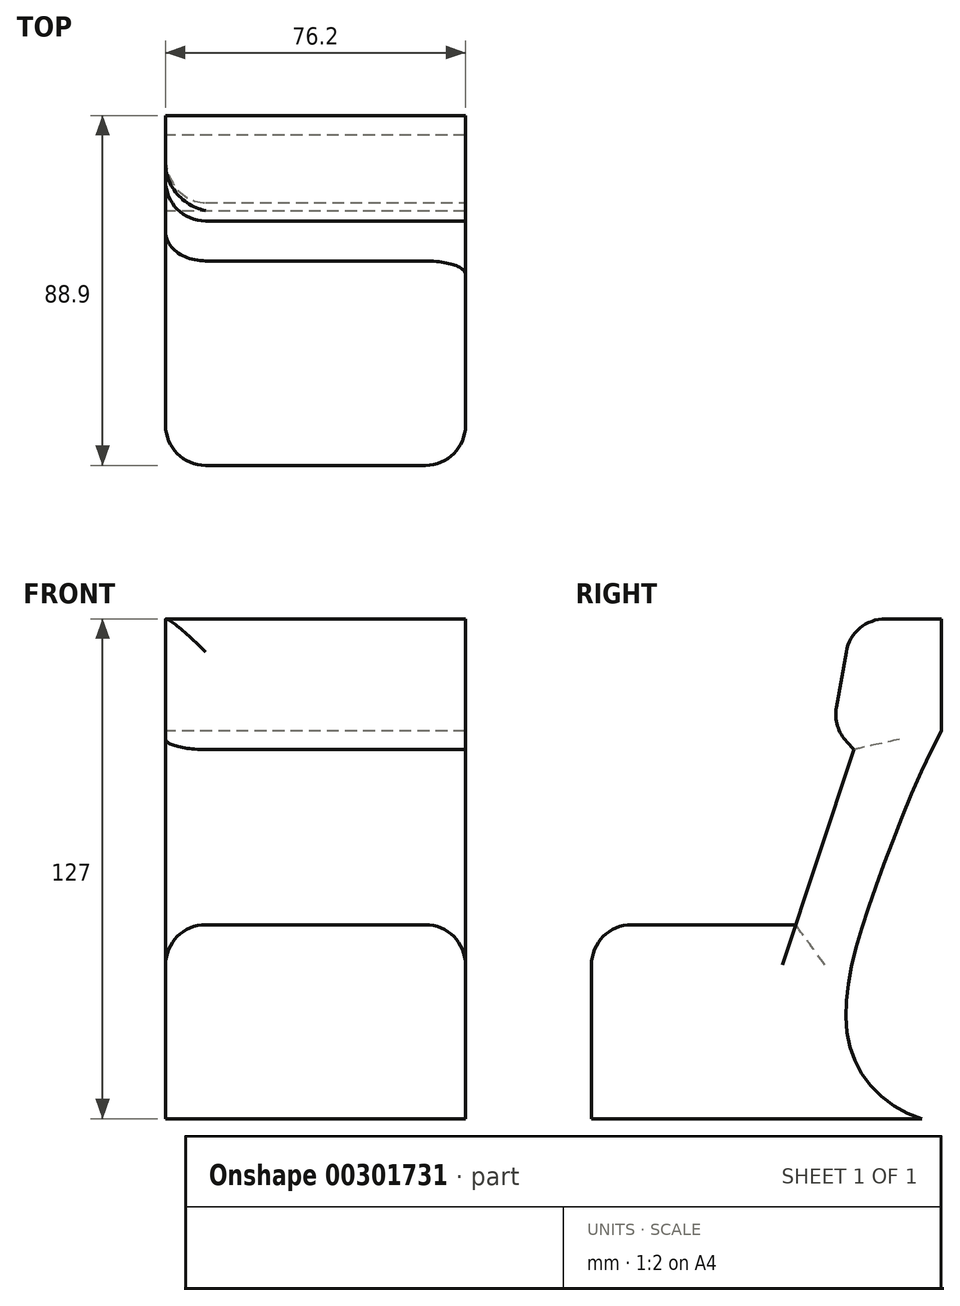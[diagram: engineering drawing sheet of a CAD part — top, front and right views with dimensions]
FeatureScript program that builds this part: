
annotation { "Feature Type Name" : "Feature", "Feature Type Description" : "" }
export const myFeature = defineFeature(function(context is Context, id is Id, definition is map)
    precondition{}
    {
        {
            var Q0;
            Q0=qCreatedBy(makeId("Top.planeOp"),FACE);
            var sketch = newSketch(context, id + "F0", { "sketchPlane" : qUnion([Q0])});
            skLineSegment(sketch, "E0.bottom", {"start": v(-38.1, 44.45) * mm, "end": v(38.1, 44.45) * mm});
            skLineSegment(sketch, "E0.top", {"start": v(-38.1, -44.45) * mm, "end": v(38.1, -44.45) * mm});
            skLineSegment(sketch, "E0.left", {"start": v(-38.1, 44.45) * mm, "end": v(-38.1, -44.45) * mm});
            skLineSegment(sketch, "E0.right", {"start": v(38.1, 44.45) * mm, "end": v(38.1, -44.45) * mm});
            skPoint(sketch, "E0.middle", {"position": v(0, 0) * mm});
            skSolve(sketch);
        }
        {
            var Q0;
            Q0=makeQuery(id+"F0.imprint","IMPRINT",FACE,{"disambiguationData":[TD([[makeQuery(id+"F0.imprint","IMPRINT",EDGE,{"derivedFrom":sQuery(id+"F0.wireOp",EDGE,"E0.bottom")}),-1.0]])]});
            extrude(context, id + "F1", {"entities" : qUnion([Q0]), "depth" : 127 * mm});
        }
        {
            var Q0;
            Q0=makeQuery(id+"F1.opExtrude","SWEPT_FACE",FACE,{"disambiguationData":[OSD([sQuery(id+"F0.wireOp",EDGE,"E0.right")])]});
            var sketch = newSketch(context, id + "F2", { "sketchPlane" : qUnion([Q0])});
            skSolve(sketch);
        }
        {
            var Q0;
            {var subQ0=sQuery(id+"F0.wireOp",EDGE,"E0.right");Q0=makeQuery(id+"F2.imprint","IMPRINT",FACE,{"disambiguationData":[TD([[makeQuery(id+"F2.imprint","IMPRINT",EDGE,{"derivedFrom":makeQuery(id+"F1.opExtrude","CAP_EDGE",EDGE,{"disambiguationData":[OSD([subQ0])],"isStart":true})}),-1.0]])]});}
            var sketch = newSketch(context, id + "F3", { "sketchPlane" : qUnion([Q0])});
            skLineSegment(sketch, "E1", {"start": v(7.48, 49.25) * mm, "end": v(-45.8, 49.25) * mm});
            skLineSegment(sketch, "E2", {"start": v(-45.8, 49.25) * mm, "end": v(-45.8, 129.88) * mm});
            skLineSegment(sketch, "E3", {"start": v(22.28, 129.88) * mm, "end": v(22.28, 127.37) * mm});
            skLineSegment(sketch, "E4", {"start": v(22.28, 129.88) * mm, "end": v(-45.8, 129.88) * mm});
            skLineSegment(sketch, "E5", {"start": v(22.28, 129.88) * mm, "end": v(16.9, 99.46) * mm});
            skLineSegment(sketch, "E6", {"start": v(16.9, 99.46) * mm, "end": v(22.28, 93.8) * mm});
            skLineSegment(sketch, "E7", {"start": v(22.28, 93.8) * mm, "end": v(7.48, 49.25) * mm});
            skPoint(sketch, "E8.start.orphan", {"position": v(22.28, 103.53) * mm});
            skSolve(sketch);
        }
        {
            var Q0;
            Q0=makeQuery(id+"F1.opExtrude","SWEPT_EDGE",EDGE,{"disambiguationData":[OSD([sQuery(id+"F0.wireOp",EDGE,"E0.top"),sQuery(id+"F0.wireOp",EDGE,"E0.left")])]});
            var Q1;
            Q1=makeQuery(id+"F1.opExtrude","SWEPT_EDGE",EDGE,{"disambiguationData":[OSD([sQuery(id+"F0.wireOp",EDGE,"E0.top"),sQuery(id+"F0.wireOp",EDGE,"E0.right")])]});
            fillet(context, id + "F4", {"entities" : qUnion([Q0, Q1]), "radius" : 10.16 * mm, "tangentPropagation" : true, "allowEdgeOverflow" : false});
        }
        {
            var Q0;
            Q0 = qSketchRegion(id + "F3", true);
            extrude(context, id + "F5", {"entities" : qUnion([Q0]), "operationType" : NewBodyOperationType.REMOVE, "endBound" : BoundingType.THROUGH_ALL, "oppositeDirection" : true, "depth" : 25.4 * mm});
        }
        {
            var Q0;
            Q0=makeQuery(id+"F1.opExtrude","SWEPT_FACE",FACE,{"disambiguationData":[OSD([sQuery(id+"F0.wireOp",EDGE,"E0.left")])]});
            var sketch = newSketch(context, id + "F6", { "sketchPlane" : qUnion([Q0])});
            skFitSpline(sketch, "E9", {"points": [v(-48.98, 121.86) * mm, v(-37.37, 73.23) * mm, v(-19.17, 29.61) * mm, v(-41.45, 0) * mm, v(-93.22, 20.83) * mm, v(-48.98, 121.86) * mm]});
            skSolve(sketch);
        }
        {
            var Q0;
            {var subQ0=sQuery(id+"F6.wireOp",EDGE,"E9");var subQ1=sQuery(id+"F0.wireOp",EDGE,"E0.left");var subQ4=makeQuery(id+"F1.opExtrude","CAP_EDGE",EDGE,{"disambiguationData":[OSD([subQ1])],"isStart":true});var subQ5=makeQuery(id+"F6.imprint","INTERSECT",VERTEX,{"derivedFrom":[subQ4,subQ0]});Q0=makeQuery(id+"F6.imprint","IMPRINT",FACE,{"disambiguationData":[TD([[makeQuery(id+"F6.imprint","IMPRINT",EDGE,{"disambiguationData":[TD([[subQ5,-1.0]])],"derivedFrom":subQ0}),-1.0]])]});}
            extrude(context, id + "F7", {"entities" : qUnion([Q0]), "operationType" : NewBodyOperationType.REMOVE, "oppositeDirection" : true, "depth" : 93.98 * mm});
        }
        {
            var Q0;
            Q0=qCreatedBy(makeId("Right.planeOp"),FACE);
            cPlane(context, id + "F8", {"entities" : qUnion([Q0]), "cplaneType" : CPlaneType.OFFSET, "offset" : 192.02 * mm, "oppositeDirection" : true, "width" : 152.4 * mm, "height" : 152.4 * mm});
        }
        {
            var Q0;
            Q0=qCreatedBy(id+"F8.planeOp",FACE);
            var sketch = newSketch(context, id + "F9", { "sketchPlane" : qUnion([Q0])});
            skFitSpline(sketch, "E10", {"points": [v(58.83, 110.77) * mm, v(29.42, 63.43) * mm, v(24.82, 10.57) * mm, v(55.62, 4.6) * mm, v(58.83, 110.77) * mm]});
            skSolve(sketch);
        }
        {
            var Q0;
            Q0=makeQuery(id+"F9.imprint","IMPRINT",FACE,{"disambiguationData":[TD([[makeQuery(id+"F9.imprint","IMPRINT",EDGE,{"derivedFrom":sQuery(id+"F9.wireOp",EDGE,"E10")}),1.0]])]});
            extrude(context, id + "F10", {"entities" : qUnion([Q0]), "operationType" : NewBodyOperationType.REMOVE, "depth" : 239 * mm});
        }
        {
            var Q0;
            Q0=makeQuery(id+"F5.boolean.opBoolean","COPY",EDGE,{"derivedFrom":makeQuery(id+"F5.opExtrude","SWEPT_EDGE",EDGE,{"disambiguationData":[OSD([sQuery(id+"F3.wireOp",EDGE,"E5"),sQuery(id+"F3.wireOp",EDGE,"E6")])]})});
            var Q1;
            Q1=makeQuery(id+"F5.boolean.opBoolean","INTERSECT",EDGE,{"derivedFrom":[makeQuery(id+"F1.opExtrude","SWEPT_FACE",FACE,{"disambiguationData":[OSD([sQuery(id+"F0.wireOp",EDGE,"E0.left")])]}),makeQuery(id+"F5.opExtrude","SWEPT_FACE",FACE,{"disambiguationData":[OSD([sQuery(id+"F3.wireOp",EDGE,"E7")])]})]});
            var Q2;
            Q2=makeQuery(id+"F5.boolean.opBoolean","COPY",EDGE,{"derivedFrom":makeQuery(id+"F5.opExtrude","CAP_EDGE",EDGE,{"disambiguationData":[OSD([sQuery(id+"F3.wireOp",EDGE,"E7")])],"isStart":true})});
            var Q3;
            Q3=makeQuery(id+"F5.boolean.opBoolean","INTERSECT",EDGE,{"derivedFrom":[makeQuery(id+"F1.opExtrude","SWEPT_FACE",FACE,{"disambiguationData":[OSD([sQuery(id+"F0.wireOp",EDGE,"E0.left")])]}),makeQuery(id+"F5.opExtrude","SWEPT_FACE",FACE,{"disambiguationData":[OSD([sQuery(id+"F3.wireOp",EDGE,"E1")])]})]});
            var Q4;
            Q4=makeQuery(id+"F5.boolean.opBoolean","INTERSECT",EDGE,{"derivedFrom":[makeQuery(id+"F1.opExtrude","SWEPT_FACE",FACE,{"disambiguationData":[OSD([sQuery(id+"F0.wireOp",EDGE,"E0.left")])]}),makeQuery(id+"F5.opExtrude","SWEPT_FACE",FACE,{"disambiguationData":[OSD([sQuery(id+"F3.wireOp",EDGE,"E5")])]})]});
            var Q5;
            Q5=makeQuery(id+"F5.boolean.opBoolean","INTERSECT",EDGE,{"derivedFrom":[makeQuery(id+"F1.opExtrude","SWEPT_FACE",FACE,{"disambiguationData":[OSD([sQuery(id+"F0.wireOp",EDGE,"E0.left")])]}),makeQuery(id+"F5.opExtrude","SWEPT_FACE",FACE,{"disambiguationData":[OSD([sQuery(id+"F3.wireOp",EDGE,"E6")])]})]});
            var Q6;
            Q6=makeQuery(id+"F5.boolean.opBoolean","COPY",EDGE,{"derivedFrom":makeQuery(id+"F5.opExtrude","CAP_EDGE",EDGE,{"disambiguationData":[OSD([sQuery(id+"F3.wireOp",EDGE,"E6")])],"isStart":true})});
            var Q7;
            Q7=makeQuery(id+"F5.boolean.opBoolean","COPY",EDGE,{"derivedFrom":makeQuery(id+"F5.opExtrude","CAP_EDGE",EDGE,{"disambiguationData":[OSD([sQuery(id+"F3.wireOp",EDGE,"E5")])],"isStart":true})});
            var Q8;
            Q8=makeQuery(id+"F5.boolean.opBoolean","INTERSECT",EDGE,{"derivedFrom":[makeQuery(id+"F1.opExtrude","CAP_FACE",FACE,{"disambiguationData":[OSD([sQuery(id+"F0.wireOp",EDGE,"E0.bottom"),sQuery(id+"F0.wireOp",EDGE,"E0.top"),sQuery(id+"F0.wireOp",EDGE,"E0.left"),sQuery(id+"F0.wireOp",EDGE,"E0.right")])],"isStart":false}),makeQuery(id+"F5.opExtrude","SWEPT_FACE",FACE,{"disambiguationData":[OSD([sQuery(id+"F3.wireOp",EDGE,"E5")])]})]});
            fillet(context, id + "F11", {"entities" : qUnion([Q0, Q1, Q2, Q3, Q4, Q5, Q6, Q7, Q8]), "radius" : 10.16 * mm, "tangentPropagation" : true, "allowEdgeOverflow" : false});
        }
    });
